# Revit family: FU_Chair_Sandler_Varya XL 0070
name_source: partatom
category: Furniture
units: mm (PartAtom-declared; Revit-internal decimal feet)

## family parameters
Always vertical = Yes
Cut with Voids When Loaded = No
OmniClass Number = 23.40.20.00
OmniClass Title = General Furniture and Specialties
Room Calculation Point = No
Shared = No
Work Plane-Based = No

## types (2) — shared parameters
Depth = 630 mm
Height = 895 mm  [stored 2.93635 ft]
Manufacturer = Sandler
Model = Varya XL 0070
URL = https://www.sandlerseating.com
Width = 640 mm  [stored 2.09974 ft]
zero-valued in all types: Default Elevation

## per-type parameters (varying)
| type | Description | Seat Visible |
| Varya XL 0070 | Swivel chair with upholstered seat pad, on polypropylene shell and 5 spoke cast aluminum swivel base fitted with Ø65mm soft tread casters. The seat height is adjustable. | Yes |
| Varya XL 0070-PP | Swivel chair with polypropylene shell and 5 spoke cast aluminum swivel base fitted with Ø65mm soft tread casters. The seat height is adjustable. Greenguard Certified. | No |

note: [stored X ft] marks values corroborated as IEEE doubles in the binary element streams (Revit-internal decimal feet)

## geometry (parser evidence)
native form markers: Sweep x12
no freeform markers — native parametric forms only
